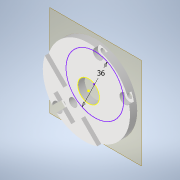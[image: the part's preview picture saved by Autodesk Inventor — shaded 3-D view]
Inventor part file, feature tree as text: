
AUTODESK INVENTOR PART (.ipt)
format: ipt  version: 2022 (Build 260153000, 153)  size: 189,440 bytes
history: native  units: in
note: dims shown in document units (in); Inventor stores cm internally (conversion verified against a paired STEP export)
features: reference x6, sketch x5, other x5, extrude x3, plane x1, hole x1
ambient origin geometry x8: Origin, YZ Plane, XZ Plane, XY Plane, X Axis, Y Axis, Z Axis, Center Point
bodies: Solid1 (feature_tree)
feature tree (21):
  plane  "Work Plane1"
  extrude  "Extrusion1"  TaperAngle=135.0deg  [1 undecoded]
  extrude  "Extrusion2"  Depth=0.0984in TaperAngle=0.0deg
  extrude  "Extrusion3"  Depth=0.1181in TaperAngle=0.0deg
  hole  "Bohrung1"  [1 undecoded]
  sketch  "Skizze5"
  sketch  "Sketch1"  dims[d0=0.2756in d1=0.0in d2=135.0deg]
  reference  "Reference1"
  reference  "Reference5"
  reference  "Reference6"
  reference  "Reference7"
  sketch  "Sketch2"  dims[d3=1.5748in d4=0.0984in d5=0.0in]
  sketch  "Sketch3"  dims[d6=0.0039in d7=0.1181in d8=0.0in]
  reference  "Reference8"
  sketch  "Skizze4"  dims[d9=0.126in d10=0.75in d11=0.2559in d12=0.2165in d13=0.5635in d14=1.0in d15=0.8108in d16=1.4173in]
  reference  "Referenz9"
  other  "<userpath>\Documents\Matchboxscope\INVENTOR\Matchboxscope_v1.iam"
  other  "Matchboxscope_v1.iam"
  other  "Matchboxscope_middle2_v1:1"
  other  "Matchboxscope_Lightperiscope_long_V0:1"
  other  "Matchboxscope_middle2_v2:1"
note: 2 required parameter values undecoded (feature->parameter linkage not recoverable at this tier; creation-order binding heuristic only, values carry confidence <= 0.55)
